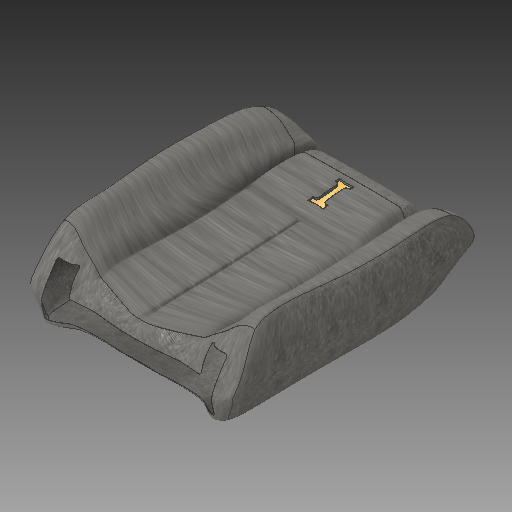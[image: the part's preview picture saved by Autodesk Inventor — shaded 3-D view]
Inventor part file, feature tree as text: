
AUTODESK INVENTOR PART (.ipt)
format: ipt  version: 2019 (Build 230136000, 136)  size: 2,768,384 bytes
history: native  units: in
note: dims shown in document units (in); Inventor stores cm internally (conversion verified against a paired STEP export)
features: sketch x11, plane x10, other x6, extrude x2, shell x1, hole x1, projected_geometry x1
ambient origin geometry x8: Origin, YZ Plane, XZ Plane, XY Plane, X Axis, Y Axis, Z Axis, Center Point
bodies: Solid7 (feature_tree)
feature tree (32):
  other  "Blocks"
  plane  "Work Plane2"
  plane  "Work Plane3"
  plane  "Work Plane4"
  plane  "Work Plane5"
  plane  "Work Plane6"
  plane  "Work Plane7"
  plane  "Work Plane8"
  sketch  "Sketch3"  dims[d22=7.0866in d23=1.9685in d24=0.9843in]
  sketch  "Sketch4"  dims[d25=3.1496in d26=-6.2992in]
  sketch  "Sketch5"  dims[d27=-3.937in d28=-11.811in]
  sketch  "Sketch6"  dims[d47=0.7874in]
  sketch  "Sketch7"  dims[d48=7.874in d49=0.0in]
  sketch  "Sketch8"  dims[d53=0.5906in]
  sketch  "Sketch9"  dims[d54=1.9685in]
  sketch  "Sketch10"  dims[d55=4.7244in]
  other  "Form3"
  plane  "Work Plane11"
  extrude  "Extrusion7"  Depth=1.9685in
  other  "Decal1"
  shell  "Shell1"  Thickness=0.9843in
  extrude  "Extrusion3"  [1 undecoded]
  plane  "Work Plane12"
  hole  "Hole1"  [1 undecoded]
  projected_geometry  "Projected Loop1"
  plane  "Work Plane10"
  sketch  "Sketch17"  dims[d76=0.0344in d77=3.937in]
  other  "Block1"
  sketch  "Sketch18"  dims[d78=0.7874in d79=0.0in]
  other  "Image2"
  sketch  "Sketch19"  dims[d94=0.0197in d95=-31.4961in d96=6.6929in d97=3.3465in d98=0.5906in d99=0.2362in d100=0.1575in d101=0.0787in d102=90.0deg d103=1.9685in d104=0.8108in d105=3.3858in d107=6.6929in d108=8.6614in d109=0.1969in d110=2.3622in]
  other  "Block1:1"
note: 2 required parameter values undecoded (feature->parameter linkage not recoverable at this tier; creation-order binding heuristic only, values carry confidence <= 0.55)
